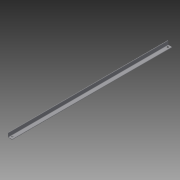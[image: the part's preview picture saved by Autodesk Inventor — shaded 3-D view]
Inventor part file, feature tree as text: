
AUTODESK INVENTOR PART (.ipt)
format: ipt  version: 2014 (Build 180170000, 170)  size: 92,160 bytes
history: native  units: in
note: dims shown in document units (in); Inventor stores cm internally (conversion verified against a paired STEP export)
features: extrude x2, sketch x2, fillet x1
ambient origin geometry x8: Origin, YZ Plane, XZ Plane, XY Plane, X Axis, Y Axis, Z Axis, Center Point
bodies: Solid1 (feature_tree)
feature tree (5):
  extrude  "Extrusion1"  Depth=0.05in
  fillet  "Fillet1"  Radius=19.0in
  extrude  "Extrusion2"  Depth=0.05in
  sketch  "Sketch1"  dims[d0=0.5in d1=0.05in d3=19.0in d4=0.0in]
  sketch  "Sketch2"  dims[d5=0.05in d6=0.196in d7=0.25in d8=0.25in d9=1.0in d10=0.0in]
